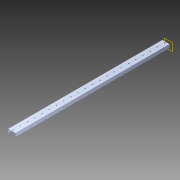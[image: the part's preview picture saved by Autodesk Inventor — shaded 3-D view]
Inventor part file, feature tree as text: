
AUTODESK INVENTOR PART (.ipt)
format: ipt  version: 2014 (Build 180170000, 170)  size: 1,286,144 bytes
history: native  units: in
note: dims shown in document units (in); Inventor stores cm internally (conversion verified against a paired STEP export)
features: extrude x3, sketch x3, pattern_circular x1, other x1, plane x1, imported_body x1, projected_geometry x1
ambient origin geometry x8: Origin, YZ Plane, XZ Plane, XY Plane, X Axis, Y Axis, Z Axis, Center Point
bodies: Body1 (feature_tree)
feature tree (11):
  pattern_circular  "CirPattern2"
  other  "217-3426-STEP1"
  plane  "Work Plane1"
  extrude  "Extrusion1"  Depth=3937.0079in TaperAngle=0.0deg
  extrude  "Extrusion2"  Depth=21.375in
  extrude  "Extrusion3"  Depth=1.0in TaperAngle=0.0deg
  imported_body  "Base1"
  sketch  "Sketch1"  dims[d0=-22.0in d1=3937.0079in d2=0.0in]
  sketch  "Sketch3"  dims[d3=21.375in d4=11.0in]
  projected_geometry  "Projected Loop1"
  sketch  "Sketch4"  dims[d5=2.0in d6=0.0in d7=1.0in d8=0.0in]
